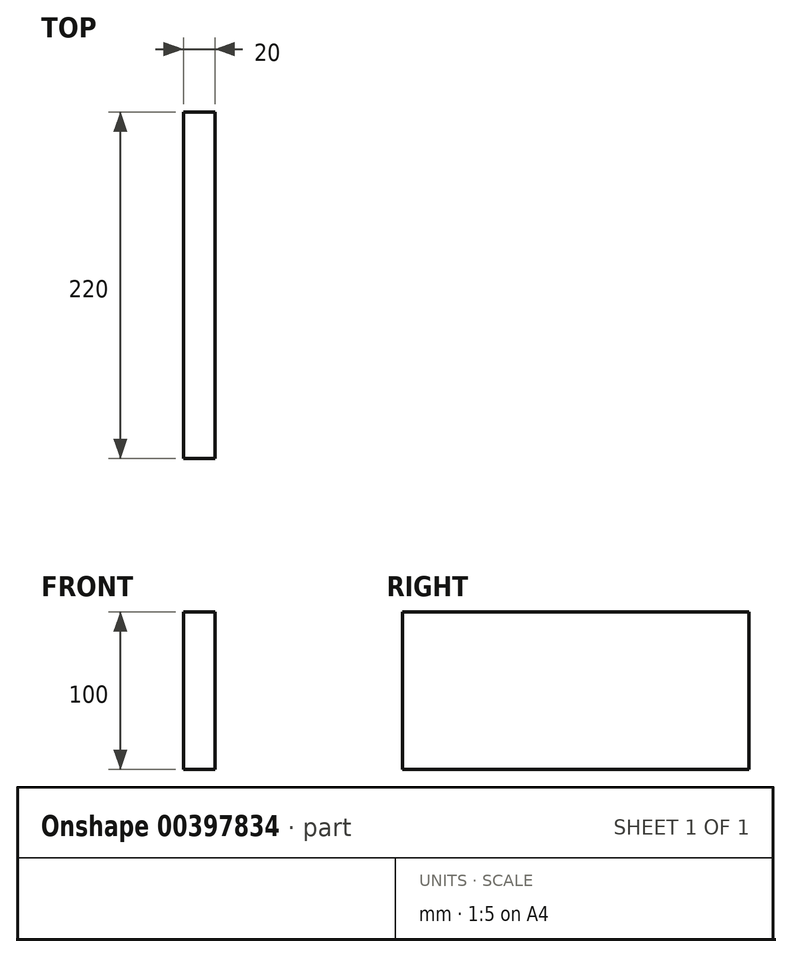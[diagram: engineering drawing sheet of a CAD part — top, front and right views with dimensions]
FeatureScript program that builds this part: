
annotation { "Feature Type Name" : "Feature", "Feature Type Description" : "" }
export const myFeature = defineFeature(function(context is Context, id is Id, definition is map)
    precondition{}
    {
        {
            var Q0;
            Q0=qCreatedBy(makeId("Top.planeOp"),FACE);
            var sketch = newSketch(context, id + "F0", { "sketchPlane" : qUnion([Q0])});
            skLineSegment(sketch, "E0.bottom", {"start": v(10, 110) * mm, "end": v(-10, 110) * mm});
            skLineSegment(sketch, "E0.top", {"start": v(10, -110) * mm, "end": v(-10, -110) * mm});
            skLineSegment(sketch, "E0.left", {"start": v(10, 110) * mm, "end": v(10, -110) * mm});
            skLineSegment(sketch, "E0.right", {"start": v(-10, 110) * mm, "end": v(-10, -110) * mm});
            skPoint(sketch, "E0.middle", {"position": v(0, 0) * mm});
            skSolve(sketch);
        }
        {
            var Q0;
            Q0 = qSketchRegion(id + "F0", true);
            extrude(context, id + "F1", {"entities" : qUnion([Q0]), "depth" : 100 * mm});
        }
    });
